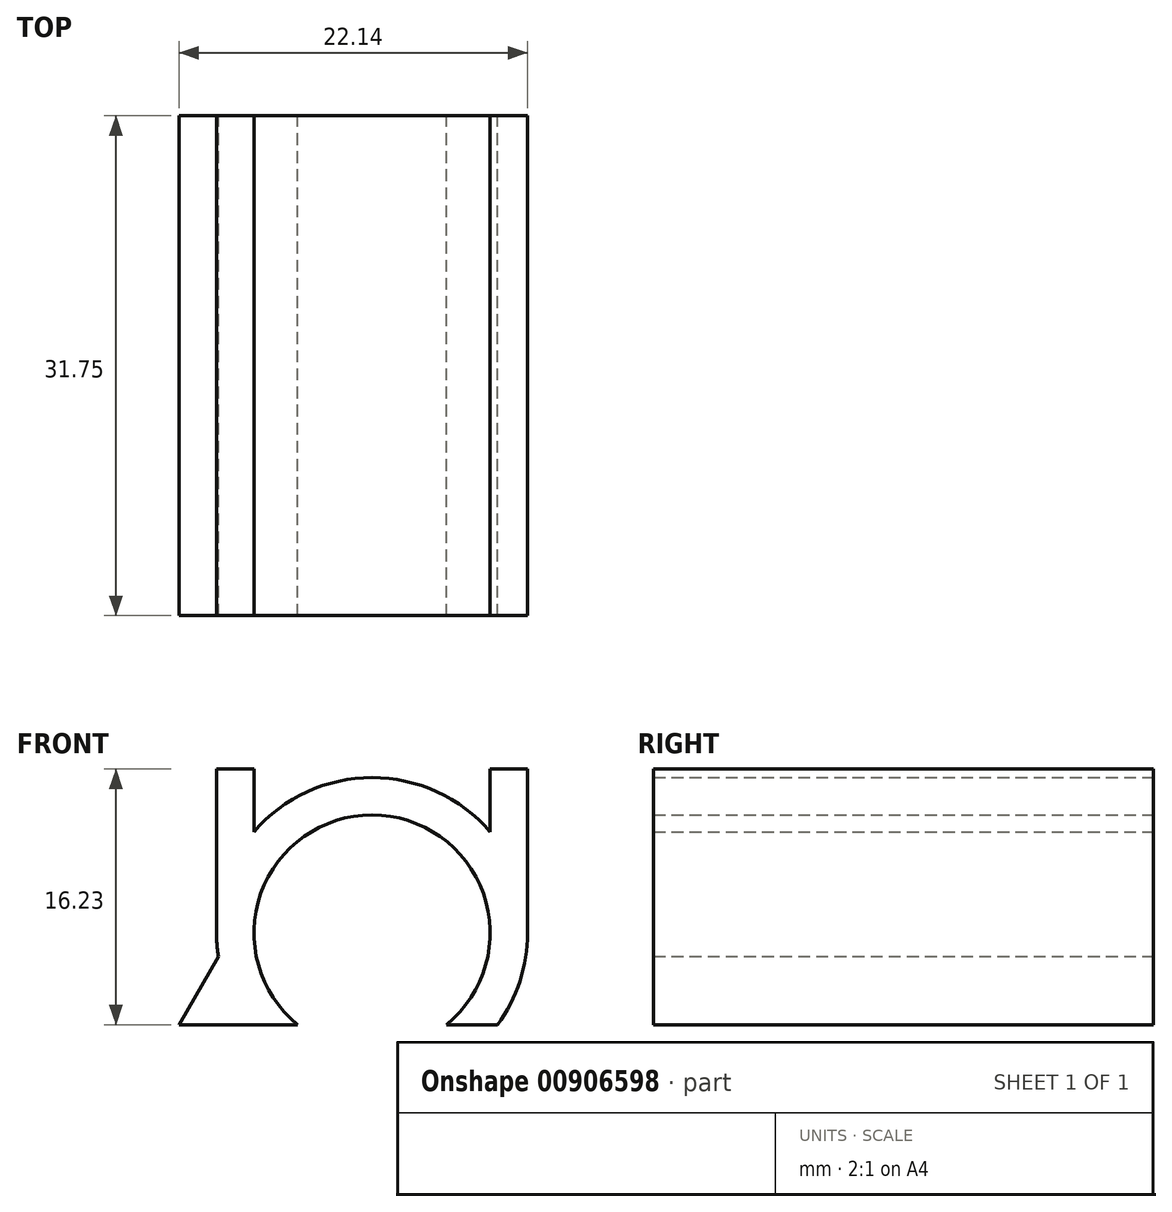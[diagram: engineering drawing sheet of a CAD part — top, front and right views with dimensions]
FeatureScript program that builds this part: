
annotation { "Feature Type Name" : "Feature", "Feature Type Description" : "" }
export const myFeature = defineFeature(function(context is Context, id is Id, definition is map)
    precondition{}
    {
        {
            var Q0;
            Q0=qCreatedBy(makeId("Front.planeOp"),FACE);
            var sketch = newSketch(context, id + "F0", { "sketchPlane" : qUnion([Q0])});
            skCircle(sketch, "E0.0", {"center": v(-12.6, 19.88) * mm, "radius": 4 * mm});
            skCircle(sketch, "E1", {"center": v(-12.6, 19.88) * mm, "radius": 7.5 * mm});
            skLineSegment(sketch, "E2", {"start": v(-20.1, 19.88) * mm, "end": v(-20.1, 30.3) * mm});
            skLineSegment(sketch, "E3", {"start": v(-5.1, 19.88) * mm, "end": v(-5.1, 30.3) * mm});
            skCircle(sketch, "E4", {"center": v(-12.6, 19.88) * mm, "radius": 9.88 * mm});
            skLineSegment(sketch, "E5", {"start": v(-22.48, 19.88) * mm, "end": v(-22.48, 30.3) * mm});
            skLineSegment(sketch, "E6", {"start": v(-2.73, 19.88) * mm, "end": v(-2.73, 30.3) * mm});
            skLineSegment(sketch, "E7", {"start": v(-22.48, 30.3) * mm, "end": v(-20.1, 30.3) * mm});
            skLineSegment(sketch, "E8", {"start": v(-5.1, 30.3) * mm, "end": v(-2.73, 30.3) * mm});
            skLineSegment(sketch, "E9.0", {"start": v(-24.87, 14.06) * mm, "end": v(-18, 25.95) * mm});
            skLineSegment(sketch, "E9.1", {"start": v(-0.43, 14.06) * mm, "end": v(-24.87, 14.06) * mm});
            skLineSegment(sketch, "E9.2", {"start": v(-0.43, 14.06) * mm, "end": v(-7.25, 25.87) * mm});
            skSolve(sketch);
        }
        {
            var Q0;
            {var subQ0=sQuery(id+"F0.wireOp",EDGE,"E9.0");var subQ1=sQuery(id+"F0.wireOp",EDGE,"E4");var subQ2=makeQuery(id+"F0.imprint","INTERSECT",VERTEX,{"derivedFrom":[subQ1,subQ0]});Q0=makeQuery(id+"F0.imprint","IMPRINT",FACE,{"disambiguationData":[TD([[makeQuery(id+"F0.imprint","IMPRINT",EDGE,{"disambiguationData":[TD([[subQ2,-1.0]])],"derivedFrom":subQ1}),-1.0]])]});}
            var Q1;
            {var subQ1=sQuery(id+"F0.wireOp",EDGE,"E2");var subQ5=sQuery(id+"F0.wireOp",EDGE,"E1");var subQ6=makeQuery(id+"F0.imprint","INTERSECT",VERTEX,{"derivedFrom":[subQ5,subQ1]});Q1=makeQuery(id+"F0.imprint","IMPRINT",FACE,{"disambiguationData":[TD([[makeQuery(id+"F0.imprint","IMPRINT",EDGE,{"disambiguationData":[TD([[subQ6,-1.0]])],"derivedFrom":subQ5}),-1.0]])]});}
            var Q2;
            {var subQ0=sQuery(id+"F0.wireOp",EDGE,"E9.0");var subQ1=sQuery(id+"F0.wireOp",EDGE,"E2");var subQ2=makeQuery(id+"F0.imprint","INTERSECT",VERTEX,{"derivedFrom":[subQ1,subQ0]});Q2=makeQuery(id+"F0.imprint","IMPRINT",FACE,{"disambiguationData":[TD([[makeQuery(id+"F0.imprint","IMPRINT",EDGE,{"disambiguationData":[TD([[subQ2,-1.0]])],"derivedFrom":subQ1}),1.0]])]});}
            var Q3;
            {var subQ4=sQuery(id+"F0.wireOp",EDGE,"E5");Q3=makeQuery(id+"F0.imprint","IMPRINT",FACE,{"disambiguationData":[TD([[makeQuery(id+"F0.imprint","IMPRINT",EDGE,{"derivedFrom":subQ4}),-1.0]])]});}
            var Q4;
            {var subQ1=sQuery(id+"F0.wireOp",EDGE,"E1");var subQ4=sQuery(id+"F0.wireOp",EDGE,"E2");var subQ5=makeQuery(id+"F0.imprint","INTERSECT",VERTEX,{"derivedFrom":[subQ1,subQ4]});Q4=makeQuery(id+"F0.imprint","IMPRINT",FACE,{"disambiguationData":[TD([[makeQuery(id+"F0.imprint","IMPRINT",EDGE,{"disambiguationData":[TD([[subQ5,1.0]])],"derivedFrom":subQ1}),-1.0]])]});}
            var Q5;
            {var subQ3=sQuery(id+"F0.wireOp",EDGE,"E1");var subQ5=sQuery(id+"F0.wireOp",EDGE,"E3");var subQ6=makeQuery(id+"F0.imprint","INTERSECT",VERTEX,{"derivedFrom":[subQ3,subQ5]});Q5=makeQuery(id+"F0.imprint","IMPRINT",FACE,{"disambiguationData":[TD([[makeQuery(id+"F0.imprint","IMPRINT",EDGE,{"disambiguationData":[TD([[subQ6,1.0]])],"derivedFrom":subQ3}),-1.0]])]});}
            var Q6;
            {var subQ0=sQuery(id+"F0.wireOp",EDGE,"E9.2");var subQ1=sQuery(id+"F0.wireOp",EDGE,"E3");var subQ2=makeQuery(id+"F0.imprint","INTERSECT",VERTEX,{"derivedFrom":[subQ1,subQ0]});Q6=makeQuery(id+"F0.imprint","IMPRINT",FACE,{"disambiguationData":[TD([[makeQuery(id+"F0.imprint","IMPRINT",EDGE,{"disambiguationData":[TD([[subQ2,-1.0]])],"derivedFrom":subQ1}),-1.0]])]});}
            var Q7;
            {var subQ0=sQuery(id+"F0.wireOp",EDGE,"E9.1");var subQ1=sQuery(id+"F0.wireOp",EDGE,"E4");var subQ2=makeQuery(id+"F0.imprint","INTERSECT",VERTEX,{"disambiguationData":[OD(1.0)],"derivedFrom":[subQ1,subQ0]});Q7=makeQuery(id+"F0.imprint","IMPRINT",FACE,{"disambiguationData":[TD([[makeQuery(id+"F0.imprint","IMPRINT",EDGE,{"disambiguationData":[TD([[subQ2,-1.0]])],"derivedFrom":subQ1}),-1.0]])]});}
            var Q8;
            {var subQ4=sQuery(id+"F0.wireOp",EDGE,"E6");Q8=makeQuery(id+"F0.imprint","IMPRINT",FACE,{"disambiguationData":[TD([[makeQuery(id+"F0.imprint","IMPRINT",EDGE,{"derivedFrom":subQ4}),1.0]])]});}
            extrude(context, id + "F1", {"entities" : qUnion([Q0, Q1, Q2, Q3, Q4, Q5, Q6, Q7, Q8]), "depth" : 31.75 * mm, "offsetDistance" : 25.4 * mm});
        }
    });
